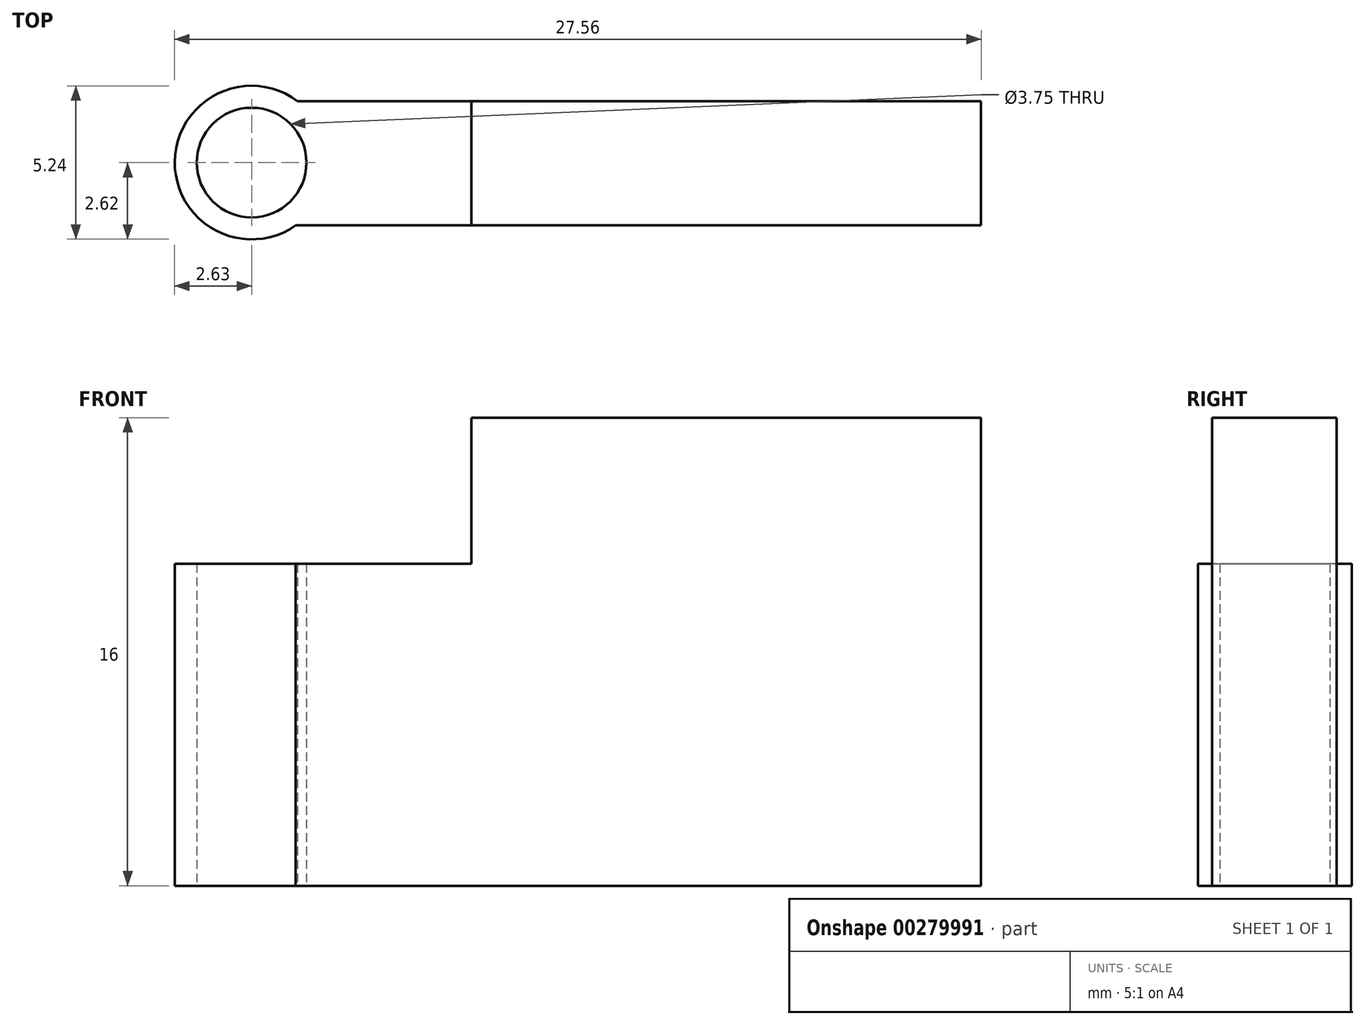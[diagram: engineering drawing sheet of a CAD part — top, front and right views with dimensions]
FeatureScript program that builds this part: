
annotation { "Feature Type Name" : "Feature", "Feature Type Description" : "" }
export const myFeature = defineFeature(function(context is Context, id is Id, definition is map)
    precondition{}
    {
        {
            var Q0;
            Q0=qCreatedBy(makeId("Top.planeOp"),FACE);
            var sketch = newSketch(context, id + "F0", { "sketchPlane" : qUnion([Q0])});
            skCircle(sketch, "E0", {"center": v(0, 0) * mm, "radius": 1.88 * mm});
            skCircle(sketch, "E1.0", {"center": v(0, 0) * mm, "radius": 2.62 * mm});
            skLineSegment(sketch, "E2.bottom", {"start": v(1.57, 2.1) * mm, "end": v(24.93, 2.1) * mm});
            skLineSegment(sketch, "E2.top", {"start": v(1.5, -2.15) * mm, "end": v(24.93, -2.15) * mm});
            skLineSegment(sketch, "E2.right", {"start": v(24.93, 2.1) * mm, "end": v(24.93, -2.15) * mm});
            skPoint(sketch, "E3.orphan", {"position": v(0, 2.1) * mm});
            skSolve(sketch);
        }
        {
            var Q0;
            Q0=makeQuery(id+"F0.imprint","IMPRINT",FACE,{"disambiguationData":[TD([[makeQuery(id+"F0.imprint","IMPRINT",EDGE,{"derivedFrom":sQuery(id+"F0.wireOp",EDGE,"E0")}),-1.0]])]});
            var Q1;
            {var subQ5=sQuery(id+"F0.wireOp",EDGE,"U0l4rMSt-DrTd-CwMe-Wu8v-vNw536Fzyvzq");Q1=makeQuery(id+"F0.imprint","IMPRINT",FACE,{"disambiguationData":[TD([[makeQuery(id+"F0.imprint","IMPRINT",EDGE,{"derivedFrom":subQ5}),1.0]])]});}
            var Q2;
            {var subQ0=sQuery(id+"F0.wireOp",EDGE,"E2.right");Q2=makeQuery(id+"F0.imprint","IMPRINT",FACE,{"disambiguationData":[TD([[makeQuery(id+"F0.imprint","IMPRINT",EDGE,{"derivedFrom":subQ0}),-1.0]])]});}
            extrude(context, id + "F1", {"entities" : qUnion([Q0, Q1, Q2]), "depth" : 11 * mm});
        }
        {
            var Q0;
            Q0=makeQuery(id+"F1.opExtrude","CAP_FACE",FACE,{"disambiguationData":[OSD([sQuery(id+"F0.wireOp",EDGE,"E0"),sQuery(id+"F0.wireOp",EDGE,"E1.0"),sQuery(id+"F0.wireOp",EDGE,"E2.bottom"),sQuery(id+"F0.wireOp",EDGE,"E2.top"),sQuery(id+"F0.wireOp",EDGE,"E2.right")])],"isStart":false});
            var sketch = newSketch(context, id + "F2", { "sketchPlane" : qUnion([Q0])});
            skLineSegment(sketch, "E4.0", {"start": v(1.5, -2.15) * mm, "end": v(24.93, -2.15) * mm});
            skLineSegment(sketch, "E5", {"start": v(7.5, -2.15) * mm, "end": v(7.5, 2.1) * mm});
            skSolve(sketch);
        }
        {
            var Q0;
            {var subQ2=sQuery(id+"F2.wireOp",EDGE,"E5");Q0=makeQuery(id+"F2.imprint","IMPRINT",FACE,{"disambiguationData":[TD([[makeQuery(id+"F2.imprint","IMPRINT",EDGE,{"derivedFrom":subQ2}),-1.0]])]});}
            extrude(context, id + "F3", {"entities" : qUnion([Q0]), "operationType" : NewBodyOperationType.ADD, "depth" : 5 * mm});
        }
    });
